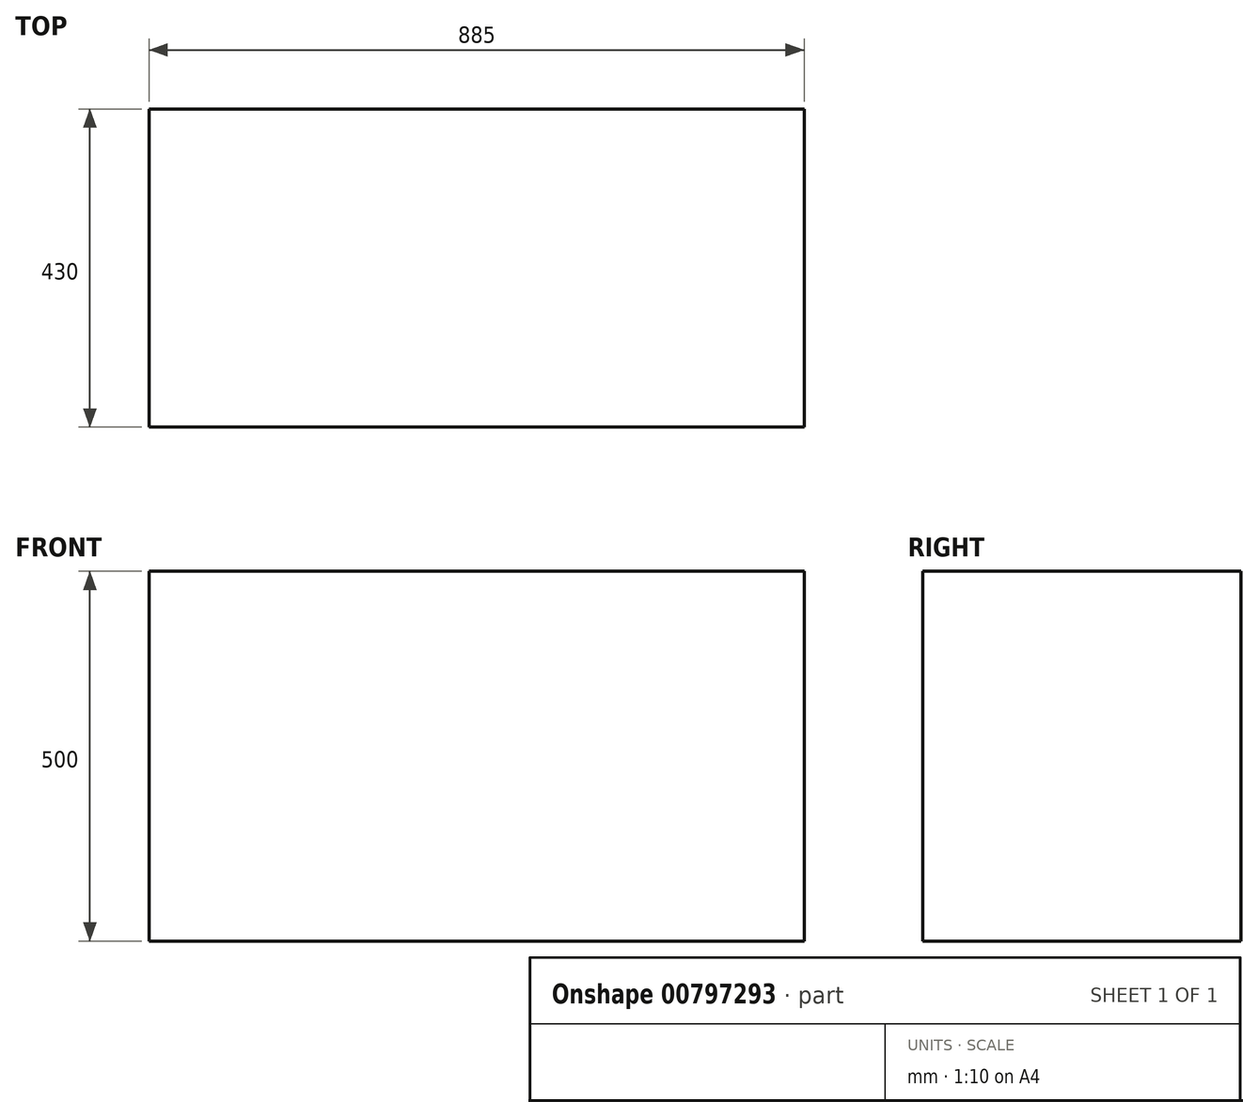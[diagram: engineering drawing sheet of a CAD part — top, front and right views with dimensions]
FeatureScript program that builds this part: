
annotation { "Feature Type Name" : "Feature", "Feature Type Description" : "" }
export const myFeature = defineFeature(function(context is Context, id is Id, definition is map)
    precondition{}
    {
        {
            var Q0;
            Q0=qCreatedBy(makeId("Front.planeOp"),FACE);
            var sketch = newSketch(context, id + "F0", { "sketchPlane" : qUnion([Q0])});
            skLineSegment(sketch, "E0.bottom", {"start": v(442.5, 250) * mm, "end": v(-442.5, 250) * mm});
            skLineSegment(sketch, "E0.top", {"start": v(442.5, -250) * mm, "end": v(-442.5, -250) * mm});
            skLineSegment(sketch, "E0.left", {"start": v(442.5, 250) * mm, "end": v(442.5, -250) * mm});
            skLineSegment(sketch, "E0.right", {"start": v(-442.5, 250) * mm, "end": v(-442.5, -250) * mm});
            skPoint(sketch, "E0.middle", {"position": v(0, 0) * mm});
            skSolve(sketch);
        }
        {
            var Q0;
            Q0 = qSketchRegion(id + "F0", true);
            extrude(context, id + "F1", {"entities" : qUnion([Q0]), "depth" : 430 * mm, "offsetDistance" : 25 * mm, "symmetric" : true});
        }
    });
